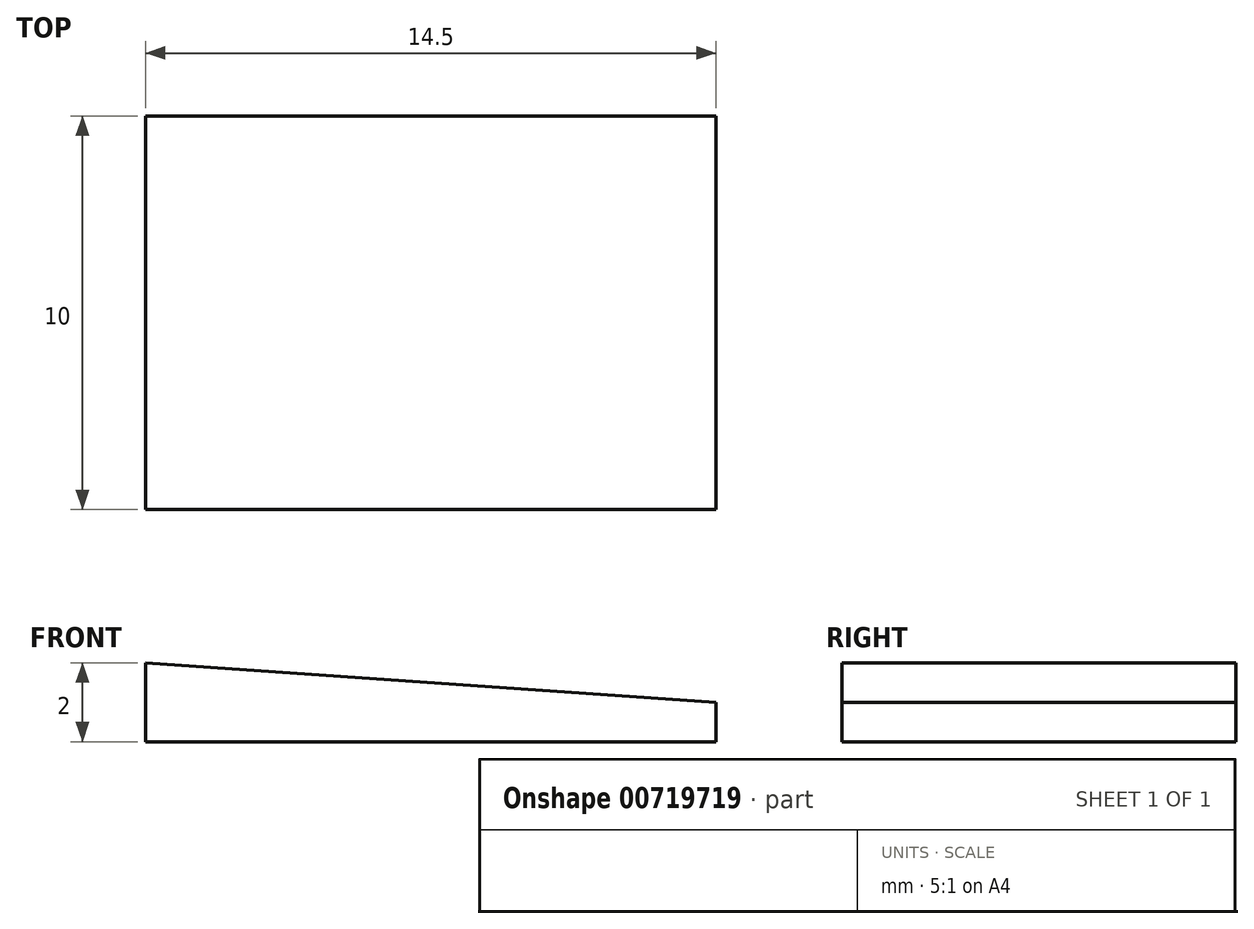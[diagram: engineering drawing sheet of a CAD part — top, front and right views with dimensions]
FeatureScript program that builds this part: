
annotation { "Feature Type Name" : "Feature", "Feature Type Description" : "" }
export const myFeature = defineFeature(function(context is Context, id is Id, definition is map)
    precondition{}
    {
        {
            var Q0;
            Q0=qCreatedBy(makeId("Top.planeOp"),FACE);
            var sketch = newSketch(context, id + "F0", { "sketchPlane" : qUnion([Q0])});
            skLineSegment(sketch, "E0.bottom", {"start": v(-7.25, 5) * mm, "end": v(7.25, 5) * mm});
            skLineSegment(sketch, "E0.top", {"start": v(-7.25, -5) * mm, "end": v(7.25, -5) * mm});
            skLineSegment(sketch, "E0.left", {"start": v(-7.25, 5) * mm, "end": v(-7.25, -5) * mm});
            skLineSegment(sketch, "E0.right", {"start": v(7.25, 5) * mm, "end": v(7.25, -5) * mm});
            skPoint(sketch, "E1", {"position": v(0, 0) * mm});
            skPoint(sketch, "E1.positionSnap0", {"position": v(0, 5) * mm});
            skPoint(sketch, "E1.positionSnap1", {"position": v(7.25, 0) * mm});
            skSolve(sketch);
        }
        {
            var Q0;
            Q0=makeQuery(id+"F0.imprint","IMPRINT",FACE,{"disambiguationData":[TD([[makeQuery(id+"F0.imprint","IMPRINT",EDGE,{"derivedFrom":sQuery(id+"F0.wireOp",EDGE,"E0.bottom")}),-1.0]])]});
            extrude(context, id + "F1", {"entities" : qUnion([Q0]), "depth" : 2 * mm, "offsetDistance" : 25 * mm});
        }
        {
            var Q0;
            Q0=makeQuery(id+"F1.opExtrude","SWEPT_FACE",FACE,{"disambiguationData":[OSD([sQuery(id+"F0.wireOp",EDGE,"E0.top")])]});
            var sketch = newSketch(context, id + "F2", { "sketchPlane" : qUnion([Q0])});
            skLineSegment(sketch, "E2", {"start": v(-7.25, 2) * mm, "end": v(7.25, 1) * mm});
            skSolve(sketch);
        }
        {
            var Q0;
            {var subQ0=sQuery(id+"F2.wireOp",EDGE,"E2");Q0=makeQuery(id+"F2.imprint","IMPRINT",FACE,{"disambiguationData":[TD([[makeQuery(id+"F2.imprint","IMPRINT",EDGE,{"derivedFrom":subQ0}),1.0]])]});}
            extrude(context, id + "F3", {"entities" : qUnion([Q0]), "operationType" : NewBodyOperationType.REMOVE, "endBound" : BoundingType.THROUGH_ALL, "oppositeDirection" : true, "depth" : 25 * mm, "offsetDistance" : 25 * mm});
        }
    });
